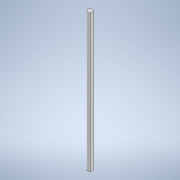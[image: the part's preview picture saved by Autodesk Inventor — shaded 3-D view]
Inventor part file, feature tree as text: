
AUTODESK INVENTOR PART (.ipt)
format: ipt  version: 2020 (Build 240168000, 168)  size: 101,376 bytes
history: native  units: in
note: dims shown in document units (in); Inventor stores cm internally (conversion verified against a paired STEP export)
features: other x3, sketch x2, extrude x1
ambient origin geometry x8: Origin, YZ Plane, XZ Plane, XY Plane, X Axis, Y Axis, Z Axis, Center Point
bodies: Solid1 (feature_tree)
feature tree (6):
  other  "634080.ipt"
  extrude  "Extrusion1"  Depth=0.3937in TaperAngle=0.0deg
  other  "Solid1::634080.ipt"
  other  "TaggingFeature1"
  sketch  "Sketch1"  dims[d0=0.3937in d1=2.0in d2=0.0in]
  sketch  "Sketch2"
